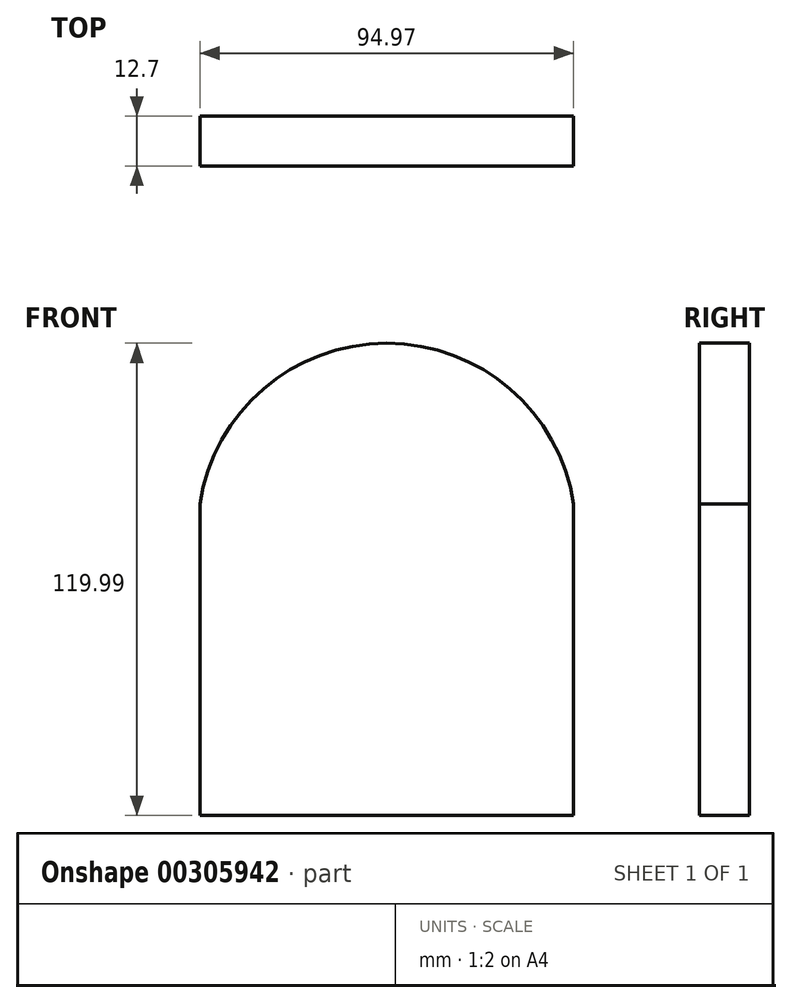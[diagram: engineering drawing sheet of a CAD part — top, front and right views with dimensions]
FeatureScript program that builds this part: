
annotation { "Feature Type Name" : "Feature", "Feature Type Description" : "" }
export const myFeature = defineFeature(function(context is Context, id is Id, definition is map)
    precondition{}
    {
        {
            var Q0;
            Q0=qCreatedBy(makeId("Front.planeOp"),FACE);
            var sketch = newSketch(context, id + "F0", { "sketchPlane" : qUnion([Q0])});
            skLineSegment(sketch, "E0", {"start": v(-46.62, -47.2) * mm, "end": v(48.35, -47.2) * mm});
            skLineSegment(sketch, "E1", {"start": v(48.35, -47.2) * mm, "end": v(48.35, 31.95) * mm});
            skLineSegment(sketch, "E2", {"start": v(-46.62, -47.2) * mm, "end": v(-46.62, 31.95) * mm});
            skArc(sketch, "E3", {"start": v(48.35, 31.95) * mm, "mid": v(0.86, 72.79) * mm, "end": v(-46.62, 31.95) * mm});
            skSolve(sketch);
        }
        {
            var Q0;
            Q0 = qSketchRegion(id + "F0", true);
            extrude(context, id + "F1", {"entities" : qUnion([Q0]), "depth" : 12.7 * mm});
        }
    });
